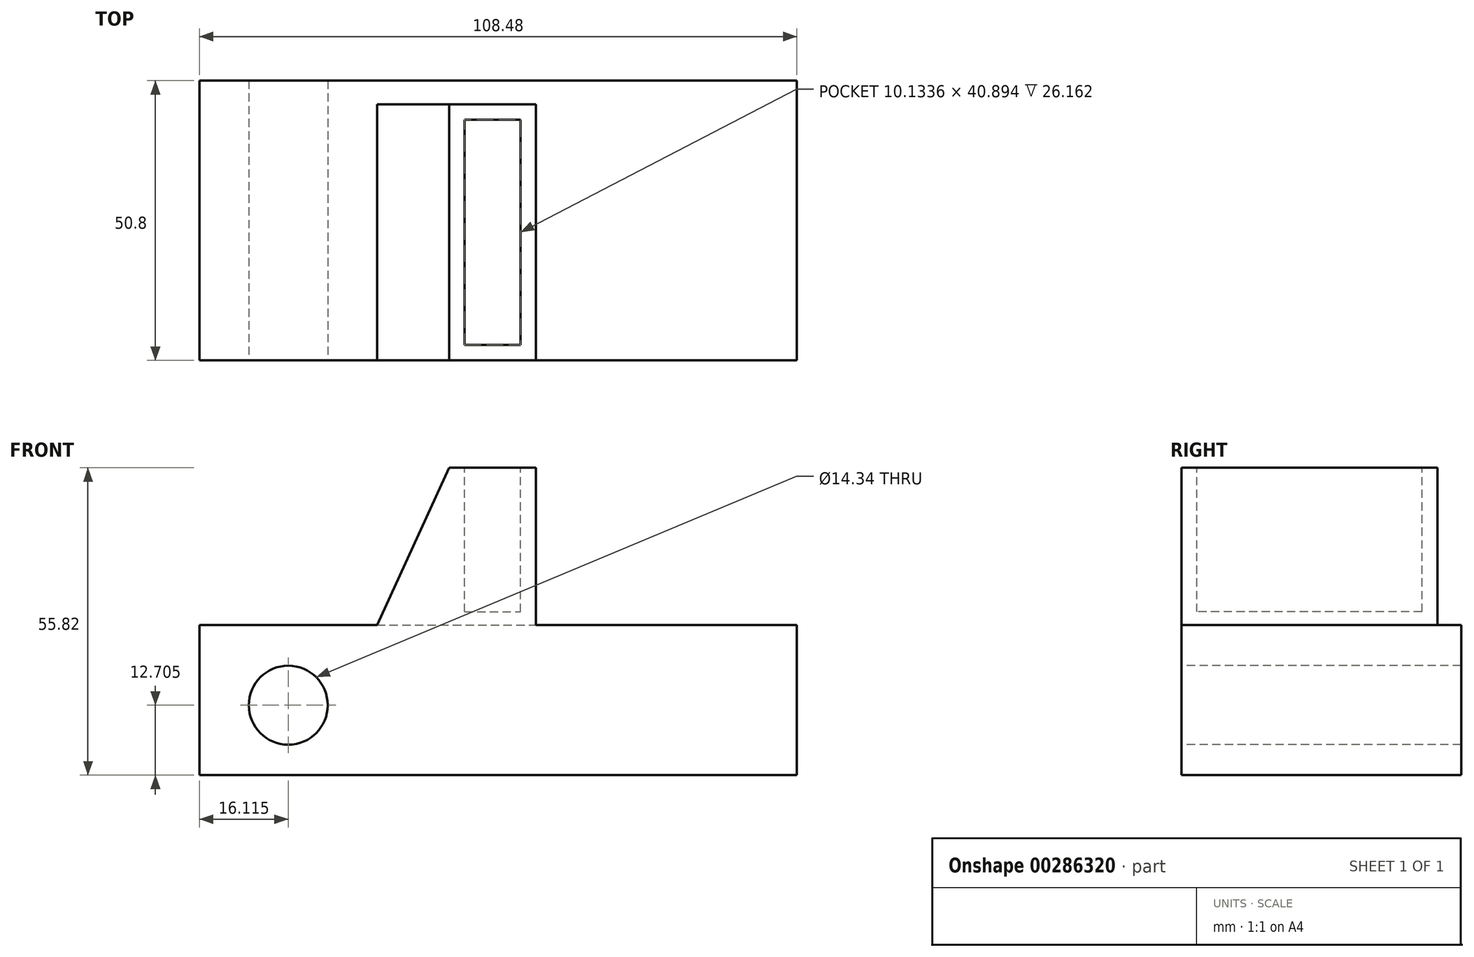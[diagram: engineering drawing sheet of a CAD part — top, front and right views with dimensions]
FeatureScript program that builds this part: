
annotation { "Feature Type Name" : "Feature", "Feature Type Description" : "" }
export const myFeature = defineFeature(function(context is Context, id is Id, definition is map)
    precondition{}
    {
        {
            var Q0;
            Q0=qCreatedBy(makeId("Front.planeOp"),FACE);
            var sketch = newSketch(context, id + "F0", { "sketchPlane" : qUnion([Q0])});
            skLineSegment(sketch, "E0.bottom", {"start": v(-52.93, 34.33) * mm, "end": v(55.55, 34.33) * mm});
            skLineSegment(sketch, "E0.top", {"start": v(-52.93, 7.07) * mm, "end": v(55.55, 7.07) * mm});
            skLineSegment(sketch, "E0.left", {"start": v(-52.93, 34.33) * mm, "end": v(-52.93, 7.07) * mm});
            skLineSegment(sketch, "E0.right", {"start": v(55.55, 34.33) * mm, "end": v(55.55, 7.07) * mm});
            skSolve(sketch);
        }
        {
            var Q0;
            Q0 = qSketchRegion(id + "F0", true);
            extrude(context, id + "F1", {"entities" : qUnion([Q0]), "depth" : 50.8 * mm});
        }
        {
            var Q0;
            Q0=makeQuery(id+"F1.opExtrude","CAP_FACE",FACE,{"disambiguationData":[OSD([sQuery(id+"F0.wireOp",EDGE,"E0.bottom"),sQuery(id+"F0.wireOp",EDGE,"E0.top"),sQuery(id+"F0.wireOp",EDGE,"E0.left"),sQuery(id+"F0.wireOp",EDGE,"E0.right")])],"isStart":false});
            var sketch = newSketch(context, id + "F2", { "sketchPlane" : qUnion([Q0])});
            skLineSegment(sketch, "E1", {"start": v(-20.7, 34.33) * mm, "end": v(-7.6, 62.89) * mm});
            skLineSegment(sketch, "E2", {"start": v(-7.6, 62.89) * mm, "end": v(8.12, 62.89) * mm});
            skLineSegment(sketch, "E3", {"start": v(8.12, 62.89) * mm, "end": v(8.12, 34.33) * mm});
            skLineSegment(sketch, "E4", {"start": v(8.12, 34.33) * mm, "end": v(-20.7, 34.33) * mm});
            skSolve(sketch);
        }
        {
            var Q0;
            Q0 = qSketchRegion(id + "F2", true);
            extrude(context, id + "F3", {"entities" : qUnion([Q0]), "operationType" : NewBodyOperationType.ADD, "oppositeDirection" : true, "depth" : 46.48 * mm});
        }
        {
            var Q0;
            Q0=makeQuery(id+"F3.boolean.opBoolean","MERGE",FACE,{"derivedFrom":[makeQuery(id+"F1.opExtrude","CAP_FACE",FACE,{"disambiguationData":[OSD([sQuery(id+"F0.wireOp",EDGE,"E0.bottom"),sQuery(id+"F0.wireOp",EDGE,"E0.top"),sQuery(id+"F0.wireOp",EDGE,"E0.left"),sQuery(id+"F0.wireOp",EDGE,"E0.right")])],"isStart":false}),makeQuery(id+"F3.opExtrude","CAP_FACE",FACE,{"disambiguationData":[OSD([sQuery(id+"F2.wireOp",EDGE,"E1"),sQuery(id+"F2.wireOp",EDGE,"E2"),sQuery(id+"F2.wireOp",EDGE,"E3"),sQuery(id+"F2.wireOp",EDGE,"E4")])],"isStart":true})]});
            var sketch = newSketch(context, id + "F4", { "sketchPlane" : qUnion([Q0])});
            skCircle(sketch, "E5", {"center": v(-36.81, 19.77) * mm, "radius": 7.17 * mm});
            skPoint(sketch, "E5.centerSnap0", {"position": v(-36.81, 34.33) * mm});
            skSolve(sketch);
        }
        {
            var Q0;
            Q0 = qSketchRegion(id + "F4", true);
            extrude(context, id + "F5", {"entities" : qUnion([Q0]), "operationType" : NewBodyOperationType.REMOVE, "endBound" : BoundingType.THROUGH_ALL, "oppositeDirection" : true, "depth" : 47.5 * mm});
        }
        {
            var Q0;
            Q0=makeQuery(id+"F3.opExtrude","SWEPT_FACE",FACE,{"disambiguationData":[OSD([sQuery(id+"F2.wireOp",EDGE,"E2")])]});
            var sketch = newSketch(context, id + "F6", { "sketchPlane" : qUnion([Q0])});
            skLineSegment(sketch, "E6.0", {"start": v(5.33, -7.11) * mm, "end": v(5.33, -48) * mm});
            skLineSegment(sketch, "E6.1", {"start": v(-4.8, -7.11) * mm, "end": v(5.33, -7.11) * mm});
            skLineSegment(sketch, "E6.2", {"start": v(-4.8, -7.11) * mm, "end": v(-4.8, -48) * mm});
            skLineSegment(sketch, "E6.3", {"start": v(-4.8, -48) * mm, "end": v(5.33, -48) * mm});
            skSolve(sketch);
        }
        {
            var Q0;
            Q0=makeQuery(id+"F6.imprint","IMPRINT",FACE,{"disambiguationData":[TD([[makeQuery(id+"F6.imprint","IMPRINT",EDGE,{"derivedFrom":sQuery(id+"F6.wireOp",EDGE,"E6.0")}),-1.0]])]});
            extrude(context, id + "F7", {"entities" : qUnion([Q0]), "operationType" : NewBodyOperationType.REMOVE, "oppositeDirection" : true, "depth" : 26.16 * mm});
        }
    });
